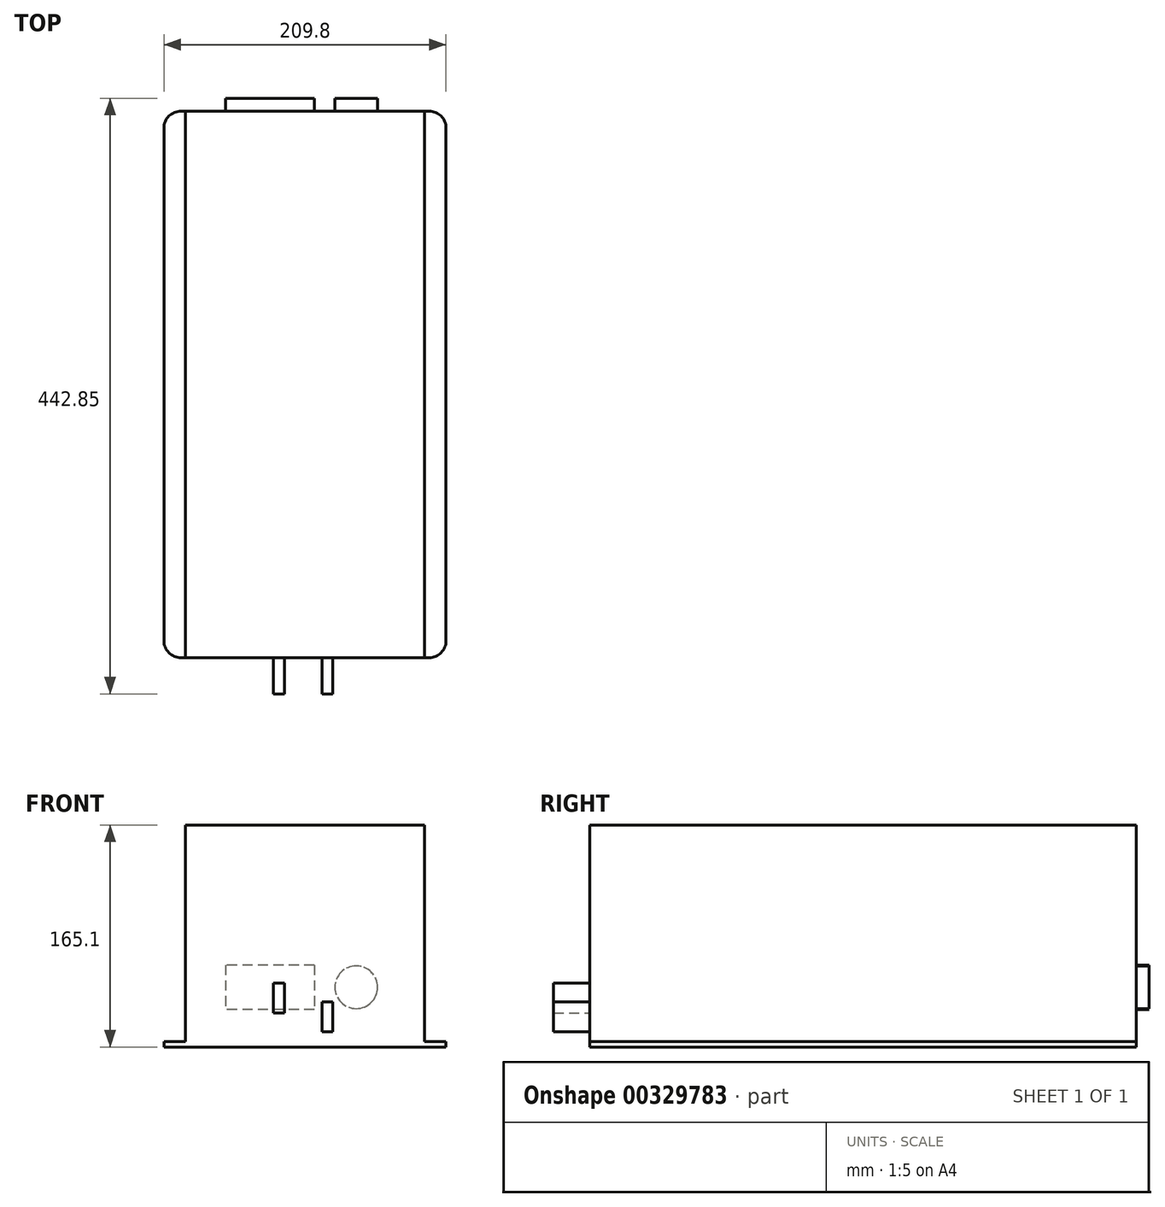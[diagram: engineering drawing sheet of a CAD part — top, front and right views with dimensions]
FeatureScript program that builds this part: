
annotation { "Feature Type Name" : "Feature", "Feature Type Description" : "" }
export const myFeature = defineFeature(function(context is Context, id is Id, definition is map)
    precondition{}
    {
        {
            var Q0;
            Q0=qCreatedBy(makeId("Front.planeOp"),FACE);
            var sketch = newSketch(context, id + "F0", { "sketchPlane" : qUnion([Q0])});
            skLineSegment(sketch, "E0.bottom", {"start": v(0, 0) * mm, "end": v(177.8, 0) * mm});
            skLineSegment(sketch, "E0.top", {"start": v(0, 165.1) * mm, "end": v(177.8, 165.1) * mm});
            skLineSegment(sketch, "E0.left", {"start": v(0, 4) * mm, "end": v(0, 165.1) * mm});
            skLineSegment(sketch, "E0.right", {"start": v(177.8, 4) * mm, "end": v(177.8, 165.1) * mm});
            skLineSegment(sketch, "E1.bottom", {"start": v(0, 0) * mm, "end": v(-16, 0) * mm});
            skLineSegment(sketch, "E1.top", {"start": v(0, 4) * mm, "end": v(-16, 4) * mm});
            skLineSegment(sketch, "E1.right", {"start": v(-16, 0) * mm, "end": v(-16, 4) * mm});
            skLineSegment(sketch, "E2.bottom", {"start": v(193.8, 0) * mm, "end": v(177.8, 0) * mm});
            skLineSegment(sketch, "E2.top", {"start": v(193.8, 4) * mm, "end": v(177.8, 4) * mm});
            skLineSegment(sketch, "E2.left", {"start": v(193.8, 0) * mm, "end": v(193.8, 4) * mm});
            skSolve(sketch);
        }
        {
            var Q0;
            Q0 = qSketchRegion(id + "F0", true);
            extrude(context, id + "F1", {"entities" : qUnion([Q0]), "depth" : 406.4 * mm});
        }
        {
            var Q0;
            Q0=makeQuery(id+"F1.opExtrude","CAP_EDGE",EDGE,{"disambiguationData":[OSD([sQuery(id+"F0.wireOp",EDGE,"E2.left")])],"isStart":true});
            var Q1;
            Q1=makeQuery(id+"F1.opExtrude","CAP_EDGE",EDGE,{"disambiguationData":[OSD([sQuery(id+"F0.wireOp",EDGE,"E2.left")])],"isStart":false});
            var Q2;
            Q2=makeQuery(id+"F1.opExtrude","CAP_EDGE",EDGE,{"disambiguationData":[OSD([sQuery(id+"F0.wireOp",EDGE,"E1.right")])],"isStart":false});
            var Q3;
            Q3=makeQuery(id+"F1.opExtrude","CAP_EDGE",EDGE,{"disambiguationData":[OSD([sQuery(id+"F0.wireOp",EDGE,"E1.right")])],"isStart":true});
            fillet(context, id + "F2", {"entities" : qUnion([Q0, Q1, Q2, Q3]), "radius" : 12.7 * mm, "tangentPropagation" : true, "allowEdgeOverflow" : false});
        }
        {
            var Q0;
            Q0=makeQuery(id+"F1.opExtrude","CAP_FACE",FACE,{"disambiguationData":[OSD([sQuery(id+"F0.wireOp",EDGE,"E0.bottom"),sQuery(id+"F0.wireOp",EDGE,"E0.top"),sQuery(id+"F0.wireOp",EDGE,"E0.left"),sQuery(id+"F0.wireOp",EDGE,"E0.right"),sQuery(id+"F0.wireOp",EDGE,"E1.bottom"),sQuery(id+"F0.wireOp",EDGE,"E1.top"),sQuery(id+"F0.wireOp",EDGE,"E1.right"),sQuery(id+"F0.wireOp",EDGE,"E2.bottom"),sQuery(id+"F0.wireOp",EDGE,"E2.top"),sQuery(id+"F0.wireOp",EDGE,"E2.left")])],"isStart":false});
            var sketch = newSketch(context, id + "F3", { "sketchPlane" : qUnion([Q0])});
            skLineSegment(sketch, "E3.bottom", {"start": v(65.53, 47.62) * mm, "end": v(73.53, 47.62) * mm});
            skLineSegment(sketch, "E3.top", {"start": v(65.53, 25.4) * mm, "end": v(73.53, 25.4) * mm});
            skLineSegment(sketch, "E3.left", {"start": v(65.53, 47.62) * mm, "end": v(65.53, 25.4) * mm});
            skLineSegment(sketch, "E3.right", {"start": v(73.53, 47.62) * mm, "end": v(73.53, 25.4) * mm});
            skLineSegment(sketch, "E4.bottom", {"start": v(101.6, 33.4) * mm, "end": v(109.6, 33.4) * mm});
            skLineSegment(sketch, "E4.top", {"start": v(101.6, 11.18) * mm, "end": v(109.6, 11.18) * mm});
            skLineSegment(sketch, "E4.left", {"start": v(101.6, 33.4) * mm, "end": v(101.6, 11.18) * mm});
            skLineSegment(sketch, "E4.right", {"start": v(109.6, 33.4) * mm, "end": v(109.6, 11.18) * mm});
            skSolve(sketch);
        }
        {
            var Q0;
            Q0 = qSketchRegion(id + "F3", true);
            extrude(context, id + "F4", {"entities" : qUnion([Q0]), "operationType" : NewBodyOperationType.ADD, "depth" : 26.92 * mm});
        }
        {
            var Q0;
            Q0=makeQuery(id+"F1.opExtrude","CAP_FACE",FACE,{"disambiguationData":[OSD([sQuery(id+"F0.wireOp",EDGE,"E0.bottom"),sQuery(id+"F0.wireOp",EDGE,"E0.top"),sQuery(id+"F0.wireOp",EDGE,"E0.left"),sQuery(id+"F0.wireOp",EDGE,"E0.right"),sQuery(id+"F0.wireOp",EDGE,"E1.bottom"),sQuery(id+"F0.wireOp",EDGE,"E1.top"),sQuery(id+"F0.wireOp",EDGE,"E1.right"),sQuery(id+"F0.wireOp",EDGE,"E2.bottom"),sQuery(id+"F0.wireOp",EDGE,"E2.top"),sQuery(id+"F0.wireOp",EDGE,"E2.left")])],"isStart":true});
            var sketch = newSketch(context, id + "F5", { "sketchPlane" : qUnion([Q0])});
            skLineSegment(sketch, "E5.bottom", {"start": v(-95.89, 60.96) * mm, "end": v(-29.84, 60.96) * mm});
            skLineSegment(sketch, "E5.top", {"start": v(-95.89, 27.94) * mm, "end": v(-29.84, 27.94) * mm});
            skLineSegment(sketch, "E5.left", {"start": v(-95.89, 60.96) * mm, "end": v(-95.89, 27.94) * mm});
            skLineSegment(sketch, "E5.right", {"start": v(-29.84, 60.96) * mm, "end": v(-29.84, 27.94) * mm});
            skCircle(sketch, "E6", {"center": v(-127, 44.45) * mm, "radius": 15.88 * mm});
            skSolve(sketch);
        }
        {
            var Q0;
            Q0 = qSketchRegion(id + "F5", true);
            extrude(context, id + "F6", {"entities" : qUnion([Q0]), "operationType" : NewBodyOperationType.ADD, "depth" : 9.52 * mm});
        }
    });
